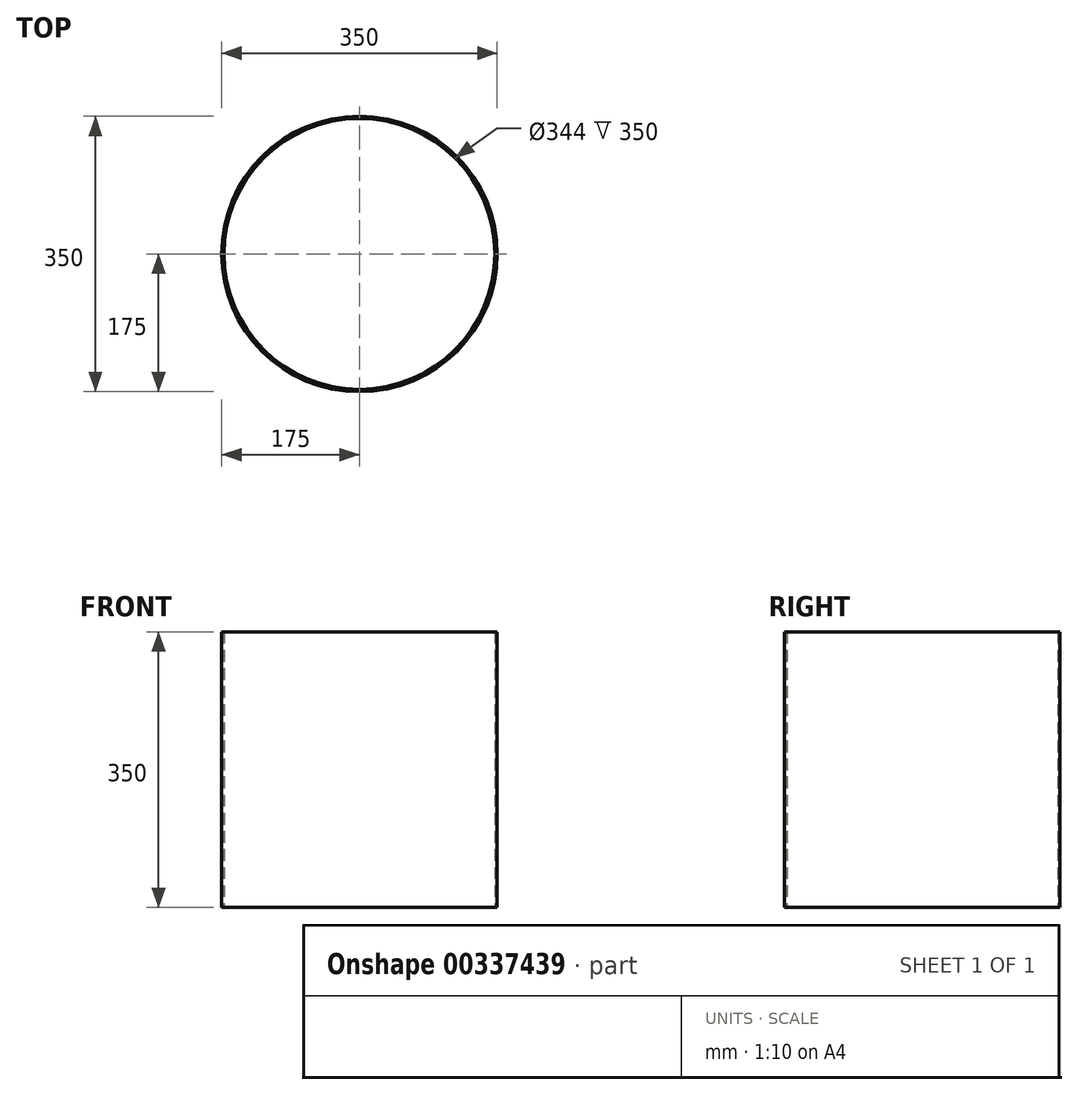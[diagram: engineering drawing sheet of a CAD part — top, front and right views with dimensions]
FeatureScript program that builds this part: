
annotation { "Feature Type Name" : "Feature", "Feature Type Description" : "" }
export const myFeature = defineFeature(function(context is Context, id is Id, definition is map)
    precondition{}
    {
        {
            var Q0;
            Q0=qCreatedBy(makeId("Top.planeOp"),FACE);
            var sketch = newSketch(context, id + "F0", { "sketchPlane" : qUnion([Q0])});
            skCircle(sketch, "E0", {"center": v(0, 0) * mm, "radius": 175 * mm});
            skCircle(sketch, "E1.0", {"center": v(0, 0) * mm, "radius": 172 * mm});
            skSolve(sketch);
        }
        {
            var Q0;
            Q0 = qSketchRegion(id + "F0", true);
            extrude(context, id + "F1", {"entities" : qUnion([Q0]), "depth" : 350 * mm});
        }
    });
